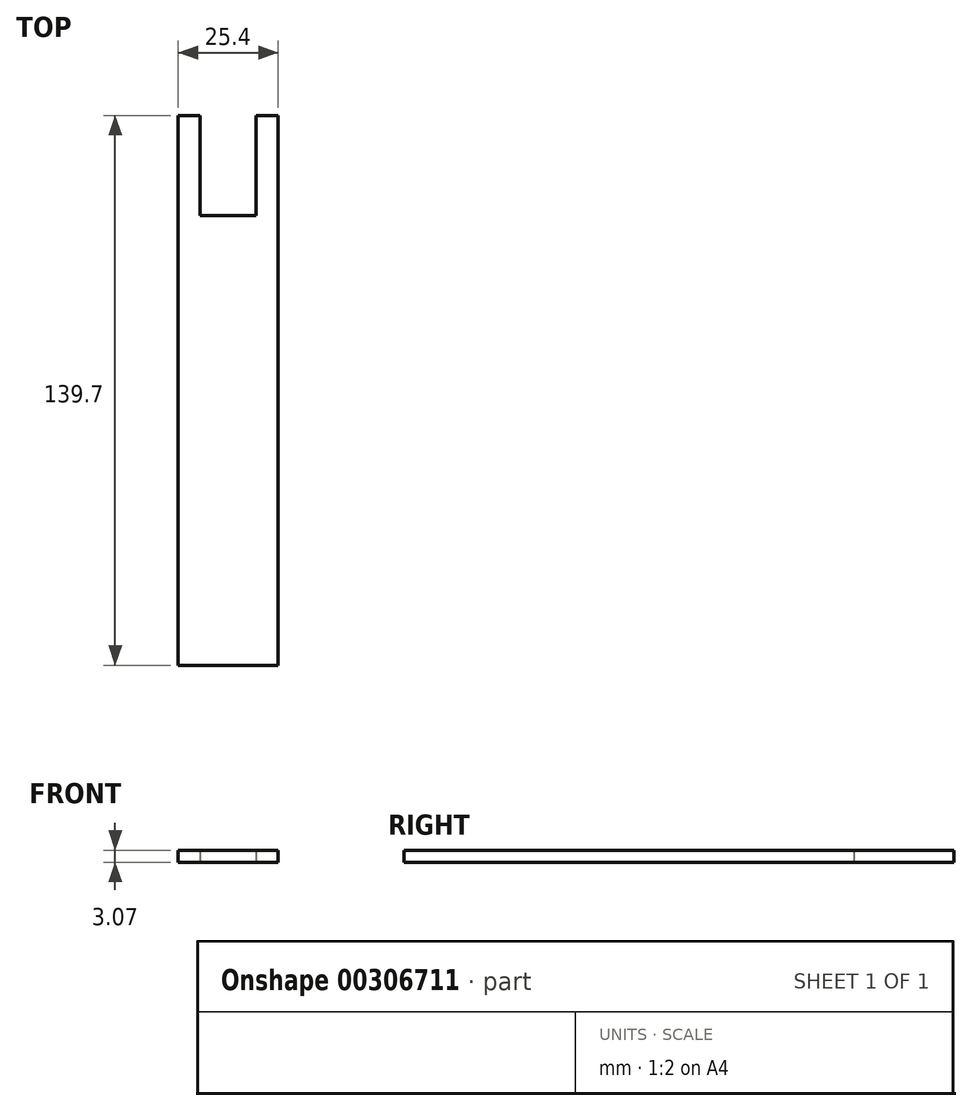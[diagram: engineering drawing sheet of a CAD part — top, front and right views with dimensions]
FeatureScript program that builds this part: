
annotation { "Feature Type Name" : "Feature", "Feature Type Description" : "" }
export const myFeature = defineFeature(function(context is Context, id is Id, definition is map)
    precondition{}
    {
        {
            var Q0;
            Q0=qCreatedBy(makeId("Top.planeOp"),FACE);
            var sketch = newSketch(context, id + "F0", { "sketchPlane" : qUnion([Q0])});
            skLineSegment(sketch, "E0.top", {"start": v(-122.8, -129.35) * mm, "end": v(-97.4, -129.35) * mm});
            skLineSegment(sketch, "E0.left", {"start": v(-122.8, 10.35) * mm, "end": v(-122.8, -129.35) * mm});
            skLineSegment(sketch, "E0.right", {"start": v(-97.4, 10.35) * mm, "end": v(-97.4, -129.35) * mm});
            skLineSegment(sketch, "E1.top", {"start": v(-117.2, -15.05) * mm, "end": v(-102.98, -15.05) * mm});
            skLineSegment(sketch, "E1.left", {"start": v(-117.2, 10.35) * mm, "end": v(-117.2, -15.05) * mm});
            skLineSegment(sketch, "E1.right", {"start": v(-102.98, 10.35) * mm, "end": v(-102.98, -15.05) * mm});
            skLineSegment(sketch, "E2", {"start": v(-122.8, 10.35) * mm, "end": v(-117.2, 10.35) * mm});
            skLineSegment(sketch, "E3", {"start": v(-102.98, 10.35) * mm, "end": v(-97.4, 10.35) * mm});
            skSolve(sketch);
        }
        {
            var Q0;
            Q0=makeQuery(id+"F0.imprint","IMPRINT",FACE,{"disambiguationData":[TD([[makeQuery(id+"F0.imprint","IMPRINT",EDGE,{"derivedFrom":sQuery(id+"F0.wireOp",EDGE,"E0.top")}),1.0]])]});
            extrude(context, id + "F1", {"entities" : qUnion([Q0]), "depth" : 3.07 * mm});
        }
    });
